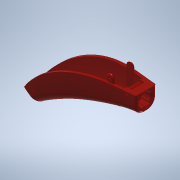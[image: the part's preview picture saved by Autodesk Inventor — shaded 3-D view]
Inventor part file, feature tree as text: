
AUTODESK INVENTOR PART (.ipt)
format: ipt  version: 2020 (Build 240168000, 168)  size: 8,566,784 bytes
history: native  units: in
note: dims shown in document units (in); Inventor stores cm internally (conversion verified against a paired STEP export)
features: fillet x16, sketch x15, extrude x14, delete_face x5, other x3, projected_geometry x3, chamfer x2, sweep x1, draft x1, mirror x1, boolean_combine x1, split x1
ambient origin geometry x8: Origin, YZ Plane, XZ Plane, XY Plane, X Axis, Y Axis, Z Axis, Center Point
bodies: Solid5 (feature_tree), Solid6 (feature_tree)
feature tree (63):
  other  "Part1b1.ipt"
  extrude  "Extrusion1"  Depth=1.1in
  sketch  "Sketch3-<F>"  dims[d18=0.625in d19=2.695in d20=0.268in d21=0.12in d22=0.3in d23=-0.0687in]
  sketch  "Sketch6-<F>"  dims[d25=0.78in d26=1.035in d30=0.18in]
  sketch  "3D Sketch2"
  sweep  "Sweep3"
  delete_face  "Delete Face22"
  delete_face  "Delete Face23"
  draft  "FaceDraft1"
  mirror  "Mirror2"
  fillet  "Fillet12"  Radius=0.975in
  fillet  "Fillet13"  Radius=0.26in
  delete_face  "Delete Face24"
  delete_face  "Delete Face25"
  fillet  "Fillet14"  Radius=0.405in
  fillet  "Fillet15"  Radius=0.725in
  extrude  "Extrusion2"  Depth=2.695in
  fillet  "Fillet16"  Radius=0.268in
  fillet  "Fillet17"  Radius=0.12in
  fillet  "Fillet18"  Radius=0.3in
  boolean_combine  "Combine3"
  extrude  "Extrusion5"  Depth=1.035in
  fillet  "Fillet19"  Radius=0.18in
  sketch  "Sketch8-<F>"  dims[d31=0.475in d32=0.7in]
  extrude  "Extrusion3"  Depth=0.7in
  extrude  "Extrusion4"  Depth=1.15in
  chamfer  "Chamfer1"  Distance=0.0412in
  sketch  "Sketch11-<F>"  dims[d33=0.975in d34=1.15in]
  extrude  "Extrusion6"  Depth=0.3937in
  fillet  "Fillet21"  Radius=0.75in
  extrude  "Extrusion7"  Depth=0.3937in
  fillet  "Fillet22"  Radius=0.425in
  sketch  "Sketch18"  dims[d7=0.78in d8=1.1in]
  split  "Split2"
  chamfer  "Chamfer4"  [1 undecoded]
  fillet  "Fillet28"  Radius=0.4947in
  extrude  "Extrusion17"  Depth=0.3937in
  fillet  "Fillet29"  Radius=0.03in
  extrude  "Extrusion11"  Depth=0.3937in
  fillet  "Fillet23"  Radius=0.0687in
  sketch  "Sketch15-<F>"  dims[d35=1.3in]
  extrude  "Extrusion12"  Depth=0.3937in
  fillet  "Fillet24"  Radius=0.475in
  extrude  "Extrusion13"  Depth=0.3937in
  delete_face  "Delete Face27"
  extrude  "Extrusion14"  Depth=0.3937in
  fillet  "Fillet26"  Radius=0.3937in
  fillet  "Fillet27"  Radius=0.08in
  extrude  "Extrusion15"  Depth=0.3937in
  extrude  "Extrusion16"  Depth=0.3937in
  sketch  "Sketch2-<F>"  dims[d36=0.1in]
  sketch  "Sketch7-<F>"  dims[d37=0.112in]
  other  "Solid1::Part1b1.ipt"
  other  "TaggingFeature1"
  sketch  "Sketch9-<F>"  dims[d38=0.14in]
  sketch  "Sketch10-<F>"  dims[d39=0.15in]
  sketch  "Sketch14-<F>"  dims[d40=0.145in]
  sketch  "Sketch16-<F>"  dims[d41=0.125in]
  projected_geometry  "Projected Loop1"
  projected_geometry  "Projected Loop2"
  sketch  "Sketch17-<F>"  dims[d42=0.09in d53=0.0412in d54=0.35in d55=0.75in d56=0.075in d57=0.425in d58=0.0in d59=0.0in d60=0.4947in d61=0.375in d62=0.03in d63=0.065in d107=0.0687in d108=0.225in d109=0.5in d110=0.625in d111=0.3937in d112=0.64in d113=0.0in d114=0.45in d115=0.1969in d116=0.7in d117=0.1969in d118=0.475in d119=0.3in d120=0.55in d121=0.1722in d122=0.08in d123=0.06in d124=0.125in d125=0.3937in d126=0.08in d127=0.06in d128=0.125in d129=0.3937in d130=0.045in d131=0.09in d132=0.115in d133=0.2461in d134=0.045in d135=0.09in d136=0.115in d137=0.2541in d139=0.052in d140=0.06in d141=0.198in d142=0.2554in d143=0.0in d144=0.008in d145=0.02in d146=0.03in d147=0.143in d148=0.1755in d149=0.023in d150=0.1in d151=0.008in d152=0.127in d153=0.108in d154=0.03in d155=0.3937in d156=0.101in d157=1.0in d158=0.0in d159=0.136in d160=0.0in d161=0.018in d162=0.016in d163=45.0deg d167=1.1501in d168=0.268in d169=1.512in d170=0.5in d171=0.7in d172=0.03in d173=0.03in d174=0.03in d175=0.166in d176=0.0in d177=0.01in d178=0.198in d179=0.2745in d180=0.5in d184=0.2752in d185=0.0in d187=0.0276in d188=0.0in d198=0.008in d199=0.008in d209=0.009in d210=0.009in d225=0.05in d226=0.125in d227=0.1374in d230=0.0362in d233=0.05in d234=0.012in d235=0.0625in d236=0.0635in d239=0.101in d240=0.0in d241=0.006in d243=0.07in d244=0.16in d245=0.317in d246=0.237in d247=0.022in d248=0.233in d249=0.0in d250=0.016in d251=0.189in d252=0.0in d253=0.05in d254=0.0in d256=0.002in d257=0.002in d258=0.275in d259=1.115in d260=0.022in d261=0.1577in d262=0.0in d263=0.15in d264=0.03in d265=0.0in d266=0.7578in d267=0.1in d268=0.0374in d272=0.1535in d273=0.189in d274=0.248in d275=0.0787in d276=0.0118in d277=0.0in d278=0.0154in d279=0.126in d280=0.0in d281=0.0039in d282=0.3436in d283=0.7559in d284=0.0079in d285=0.0004in d286=0.0079in d287=0.0079in]
  sketch  "Sketch19"  dims[d10=1.0in d13=2.75in d14=0.975in d15=0.26in d16=0.405in d17=0.725in]
  projected_geometry  "Projected Loop4"
note: 1 required parameter value undecoded (feature->parameter linkage not recoverable at this tier; creation-order binding heuristic only, values carry confidence <= 0.55)
